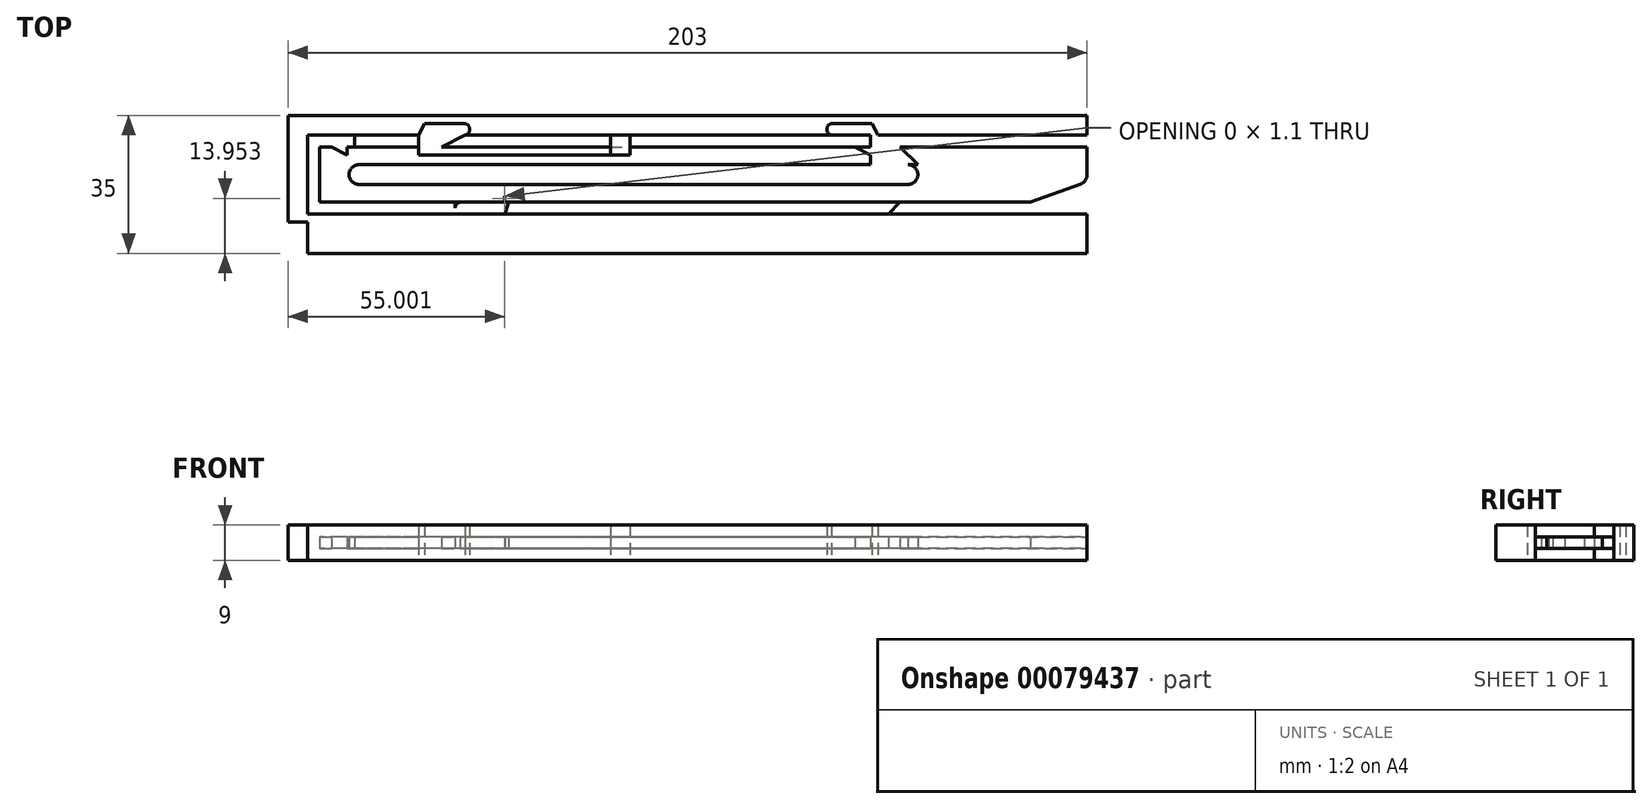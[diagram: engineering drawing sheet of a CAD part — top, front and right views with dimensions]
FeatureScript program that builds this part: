
annotation { "Feature Type Name" : "Feature", "Feature Type Description" : "" }
export const myFeature = defineFeature(function(context is Context, id is Id, definition is map)
    precondition{}
    {
        {
            var Q0;
            Q0=qCreatedBy(makeId("Top.planeOp"),FACE);
            var sketch = newSketch(context, id + "F0", { "sketchPlane" : qUnion([Q0])});
            skLineSegment(sketch, "E0.bottom", {"start": v(-77.5, 10) * mm, "end": v(77.5, 10) * mm, "construction": true});
            skLineSegment(sketch, "E0.top", {"start": v(-77.5, -10) * mm, "end": v(77.5, -10) * mm, "construction": true});
            skLineSegment(sketch, "E0.left", {"start": v(-77.5, 10) * mm, "end": v(-77.5, -10) * mm, "construction": true});
            skLineSegment(sketch, "E0.right", {"start": v(77.5, 10) * mm, "end": v(77.5, -10) * mm, "construction": true});
            skPoint(sketch, "E0.middle", {"position": v(0, 0) * mm});
            skLineSegment(sketch, "E1.bottom", {"start": v(-77.5, -2.5) * mm, "end": v(77.5, -2.5) * mm, "construction": true});
            skLineSegment(sketch, "E1.top", {"start": v(-77.5, 2.5) * mm, "end": v(77.5, 2.5) * mm, "construction": true});
            skLineSegment(sketch, "E1.left", {"start": v(-77.5, -2.5) * mm, "end": v(-77.5, 2.5) * mm, "construction": true});
            skLineSegment(sketch, "E1.right", {"start": v(77.5, -2.5) * mm, "end": v(77.5, 2.5) * mm, "construction": true});
            skLineSegment(sketch, "E2.top", {"start": v(-77.5, 7) * mm, "end": v(77.5, 7) * mm, "construction": true});
            skLineSegment(sketch, "E2.left", {"start": v(-77.5, 10) * mm, "end": v(-77.5, 7) * mm, "construction": true});
            skLineSegment(sketch, "E2.right", {"start": v(77.5, 10) * mm, "end": v(77.5, 7) * mm, "construction": true});
            skLineSegment(sketch, "E3", {"start": v(-77.5, 10) * mm, "end": v(-67.5, 7) * mm});
            skLineSegment(sketch, "E4", {"start": v(-67.5, 7) * mm, "end": v(-67.5, 10) * mm});
            skLineSegment(sketch, "E5", {"start": v(-67.5, 10) * mm, "end": v(-47.5, 10) * mm});
            skLineSegment(sketch, "E6.top", {"start": v(-77.5, -7) * mm, "end": v(77.5, -7) * mm, "construction": true});
            skLineSegment(sketch, "E6.left", {"start": v(-77.5, -10) * mm, "end": v(-77.5, -7) * mm, "construction": true});
            skLineSegment(sketch, "E6.right", {"start": v(77.5, -10) * mm, "end": v(77.5, -7) * mm, "construction": true});
            skLineSegment(sketch, "E7", {"start": v(-77.5, -10) * mm, "end": v(-77.5, -2.5) * mm});
            skLineSegment(sketch, "E8", {"start": v(77.5, -2.5) * mm, "end": v(70, -10) * mm});
            skLineSegment(sketch, "E9", {"start": v(77.5, 2.5) * mm, "end": v(70, 10) * mm});
            skLineSegment(sketch, "E10", {"start": v(70, 10) * mm, "end": v(-37.5, 10) * mm});
            skLineSegment(sketch, "E11", {"start": v(-43.17, 2.5) * mm, "end": v(-43.17, -2.5) * mm, "construction": true});
            skLineSegment(sketch, "E12", {"start": v(77.5, -2.5) * mm, "end": v(-43.17, -2.5) * mm});
            skLineSegment(sketch, "E13", {"start": v(77.5, 2.5) * mm, "end": v(-43.17, 2.5) * mm});
            skLineSegment(sketch, "E14", {"start": v(-77.5, 2.5) * mm, "end": v(-77.5, 10) * mm});
            skLineSegment(sketch, "E15", {"start": v(70, -10) * mm, "end": v(-77.5, -10) * mm});
            skLineSegment(sketch, "E16", {"start": v(-37.5, 10) * mm, "end": v(-47.5, 5) * mm});
            skLineSegment(sketch, "E17", {"start": v(-47.5, 10) * mm, "end": v(-47.5, 5) * mm});
            skArc(sketch, "E18", {"start": v(-77.5, -2.5) * mm, "mid": v(-75, 0) * mm, "end": v(-77.5, 2.5) * mm});
            skArc(sketch, "E19", {"start": v(-43.17, 2.5) * mm, "mid": v(-45.67, 0) * mm, "end": v(-43.17, -2.5) * mm});
            skSolve(sketch);
        }
        {
            var Q0;
            Q0=makeQuery(id+"F0.imprint","IMPRINT",FACE,{"disambiguationData":[TD([[makeQuery(id+"F0.imprint","IMPRINT",EDGE,{"derivedFrom":sQuery(id+"F0.wireOp",EDGE,"E3")}),-1.0]])]});
            var sketch = newSketch(context, id + "F1", { "sketchPlane" : qUnion([Q0])});
            skLineSegment(sketch, "E20.bottom", {"start": v(-161.47, 129.05) * mm, "end": v(-6.47, 129.05) * mm, "construction": true});
            skLineSegment(sketch, "E20.top", {"start": v(-161.47, 109.05) * mm, "end": v(-6.47, 109.05) * mm, "construction": true});
            skLineSegment(sketch, "E20.left", {"start": v(-161.47, 129.05) * mm, "end": v(-161.47, 109.05) * mm, "construction": true});
            skLineSegment(sketch, "E20.right", {"start": v(-6.47, 129.05) * mm, "end": v(-6.47, 109.05) * mm, "construction": true});
            skPoint(sketch, "E20.middle", {"position": v(-83.97, 119.05) * mm});
            skLineSegment(sketch, "E21.bottom", {"start": v(-161.47, 116.55) * mm, "end": v(-6.47, 116.55) * mm, "construction": true});
            skLineSegment(sketch, "E21.top", {"start": v(-161.47, 121.55) * mm, "end": v(-6.47, 121.55) * mm, "construction": true});
            skLineSegment(sketch, "E21.left", {"start": v(-161.47, 116.55) * mm, "end": v(-161.47, 121.55) * mm, "construction": true});
            skLineSegment(sketch, "E21.right", {"start": v(-6.47, 116.55) * mm, "end": v(-6.47, 121.55) * mm, "construction": true});
            skLineSegment(sketch, "E22.top", {"start": v(-161.47, 126.05) * mm, "end": v(-6.47, 126.05) * mm, "construction": true});
            skLineSegment(sketch, "E22.left", {"start": v(-161.47, 129.05) * mm, "end": v(-161.47, 126.05) * mm, "construction": true});
            skLineSegment(sketch, "E22.right", {"start": v(-6.47, 129.05) * mm, "end": v(-6.47, 126.05) * mm, "construction": true});
            skLineSegment(sketch, "E23", {"start": v(-151.47, 129.05) * mm, "end": v(-133.36, 129.05) * mm});
            skLineSegment(sketch, "E24.top", {"start": v(-161.47, 112.05) * mm, "end": v(-6.47, 112.05) * mm, "construction": true});
            skLineSegment(sketch, "E24.left", {"start": v(-161.47, 109.05) * mm, "end": v(-161.47, 112.05) * mm, "construction": true});
            skLineSegment(sketch, "E24.right", {"start": v(-6.47, 109.05) * mm, "end": v(-6.47, 112.05) * mm, "construction": true});
            skLineSegment(sketch, "E25", {"start": v(-161.47, 109.05) * mm, "end": v(-161.47, 116.55) * mm});
            skLineSegment(sketch, "E26", {"start": v(-6.47, 116.55) * mm, "end": v(-13.97, 109.05) * mm});
            skLineSegment(sketch, "E27", {"start": v(-6.47, 121.55) * mm, "end": v(-13.97, 129.05) * mm});
            skLineSegment(sketch, "E28", {"start": v(-13.97, 129.05) * mm, "end": v(-16.59, 129.05) * mm});
            skLineSegment(sketch, "E29", {"start": v(-127.14, 121.55) * mm, "end": v(-127.14, 116.55) * mm, "construction": true});
            skLineSegment(sketch, "E30", {"start": v(-6.47, 116.55) * mm, "end": v(-127.14, 116.55) * mm});
            skLineSegment(sketch, "E31", {"start": v(-6.47, 121.55) * mm, "end": v(-127.14, 121.55) * mm});
            skLineSegment(sketch, "E32", {"start": v(-161.47, 121.55) * mm, "end": v(-161.47, 129.05) * mm});
            skLineSegment(sketch, "E33", {"start": v(-13.97, 109.05) * mm, "end": v(-111.47, 109.05) * mm});
            skLineSegment(sketch, "E34", {"start": v(-121.16, 129.2) * mm, "end": v(-131.47, 124.05) * mm});
            skLineSegment(sketch, "E35", {"start": v(-131.47, 129.05) * mm, "end": v(-131.47, 124.05) * mm, "construction": true});
            skArc(sketch, "E36", {"start": v(-161.47, 116.55) * mm, "mid": v(-158.97, 119.05) * mm, "end": v(-161.47, 121.55) * mm});
            skArc(sketch, "E37", {"start": v(-127.14, 121.55) * mm, "mid": v(-129.64, 119.05) * mm, "end": v(-127.14, 116.55) * mm});
            skLineSegment(sketch, "E38.left", {"start": v(-158.47, 126.05) * mm, "end": v(-158.47, 112.05) * mm, "construction": true});
            skLineSegment(sketch, "E39", {"start": v(-158.47, 119.05) * mm, "end": v(36.53, 119.05) * mm, "construction": true});
            skLineSegment(sketch, "E40", {"start": v(-158.47, 126.05) * mm, "end": v(36.53, 126.05) * mm, "construction": true});
            skLineSegment(sketch, "E41", {"start": v(36.53, 126.05) * mm, "end": v(36.53, 112.05) * mm, "construction": true});
            skLineSegment(sketch, "E42", {"start": v(36.53, 112.05) * mm, "end": v(-158.47, 112.05) * mm, "construction": true});
            skArc(sketch, "E43", {"start": v(34.88, 116.7) * mm, "mid": v(36.53, 119.05) * mm, "end": v(34.88, 121.4) * mm});
            skLineSegment(sketch, "E44", {"start": v(34.88, 121.4) * mm, "end": v(22.1, 126.05) * mm});
            skLineSegment(sketch, "E45", {"start": v(34.88, 116.7) * mm, "end": v(22.1, 112.05) * mm});
            skArc(sketch, "E46", {"start": v(34.88, 121.4) * mm, "mid": v(31.53, 119.05) * mm, "end": v(34.88, 116.7) * mm, "construction": true});
            skLineSegment(sketch, "E47", {"start": v(-158.47, 126.05) * mm, "end": v(-133.36, 126.05) * mm});
            skLineSegment(sketch, "E48", {"start": v(-131.47, 124.05) * mm, "end": v(-127.48, 126.05) * mm});
            skLineSegment(sketch, "E49", {"start": v(-81.47, 126.05) * mm, "end": v(22.1, 126.05) * mm});
            skLineSegment(sketch, "E50", {"start": v(22.1, 112.05) * mm, "end": v(-158.47, 112.05) * mm});
            skLineSegment(sketch, "E51", {"start": v(-158.47, 126.05) * mm, "end": v(-158.47, 112.05) * mm});
            skLineSegment(sketch, "E52", {"start": v(-111.47, 126.05) * mm, "end": v(-111.47, 112.05) * mm, "construction": true});
            skLineSegment(sketch, "E53", {"start": v(-114.47, 113.55) * mm, "end": v(-158.47, 113.55) * mm, "construction": true});
            skLineSegment(sketch, "E54", {"start": v(-81.47, 124.05) * mm, "end": v(-81.47, 126.05) * mm});
            skLineSegment(sketch, "E55.trimOffspring", {"start": v(-81.47, 124.05) * mm, "end": v(27.6, 124.05) * mm, "construction": true});
            skLineSegment(sketch, "E56", {"start": v(-81.47, 124.05) * mm, "end": v(-131.47, 124.05) * mm});
            skLineSegment(sketch, "E57", {"start": v(-131.47, 126.05) * mm, "end": v(-131.47, 124.05) * mm});
            skLineSegment(sketch, "E58", {"start": v(-113.42, 114.98) * mm, "end": v(-122.97, 111.98) * mm});
            skLineSegment(sketch, "E59", {"start": v(-122.07, 109.12) * mm, "end": v(-112.52, 112.12) * mm});
            skLineSegment(sketch, "E60", {"start": v(-111.47, 112.05) * mm, "end": v(-111.47, 109.05) * mm});
            skLineSegment(sketch, "E61", {"start": v(-124.02, 112.05) * mm, "end": v(-124.02, 110.05) * mm});
            skCircle(sketch, "E62", {"center": v(-122.52, 110.55) * mm, "radius": 0.5 * mm, "construction": true});
            skCircle(sketch, "E63", {"center": v(-112.97, 113.55) * mm, "radius": 0.5 * mm, "construction": true});
            skLineSegment(sketch, "E64.0", {"start": v(-111.48, 113.5) * mm, "end": v(-117.04, 111.75) * mm, "construction": true});
            skLineSegment(sketch, "E65.0", {"start": v(-111.6, 112.93) * mm, "end": v(-116.9, 111.27) * mm, "construction": true});
            skLineSegment(sketch, "E66", {"start": v(-124.02, 109.55) * mm, "end": v(-129.02, 109.55) * mm, "construction": true});
            skLineSegment(sketch, "E67", {"start": v(-124.02, 110.05) * mm, "end": v(-139.02, 110.05) * mm});
            skLineSegment(sketch, "E68", {"start": v(-139.02, 109.55) * mm, "end": v(-139.02, 110.05) * mm});
            skLineSegment(sketch, "E69", {"start": v(-129.02, 109.05) * mm, "end": v(-129.02, 109.55) * mm});
            skLineSegment(sketch, "E70", {"start": v(-129.02, 109.55) * mm, "end": v(-139.02, 109.55) * mm});
            skLineSegment(sketch, "E71", {"start": v(-129.02, 109.05) * mm, "end": v(-161.47, 109.05) * mm});
            skLineSegment(sketch, "E72", {"start": v(-111.47, 109.05) * mm, "end": v(-129.02, 109.05) * mm, "construction": true});
            skLineSegment(sketch, "E73", {"start": v(-124.02, 110.05) * mm, "end": v(-124.02, 109.05) * mm, "construction": true});
            skArc(sketch, "E74", {"start": v(-123.72, 109.65) * mm, "mid": v(-123.52, 109.43) * mm, "end": v(-123.29, 109.26) * mm});
            skArc(sketch, "E75", {"start": v(-123.29, 109.26) * mm, "mid": v(-122.7, 109.06) * mm, "end": v(-122.07, 109.12) * mm});
            skArc(sketch, "E76", {"start": v(-121.02, 110.5) * mm, "mid": v(-121.6, 111.74) * mm, "end": v(-122.97, 111.98) * mm, "construction": true});
            skArc(sketch, "E77", {"start": v(-121.15, 109.93) * mm, "mid": v(-121.06, 110.2) * mm, "end": v(-121.02, 110.5) * mm, "construction": true});
            skLineSegment(sketch, "E78", {"start": v(-151.47, 129.05) * mm, "end": v(-151.47, 124.05) * mm});
            skLineSegment(sketch, "E79", {"start": v(-151.47, 124.05) * mm, "end": v(-161.47, 129.05) * mm});
            skPoint(sketch, "E80", {"position": v(-166.47, 104.05) * mm});
            skLineSegment(sketch, "E81", {"start": v(-166.47, 104.05) * mm, "end": v(36.53, 104.05) * mm});
            skPoint(sketch, "E82", {"position": v(-166.47, 134.05) * mm});
            skLineSegment(sketch, "E83", {"start": v(-166.47, 134.05) * mm, "end": v(36.53, 134.05) * mm});
            skLineSegment(sketch, "E84", {"start": v(36.53, 134.05) * mm, "end": v(-166.47, 134.05) * mm});
            skLineSegment(sketch, "E85", {"start": v(-166.47, 104.05) * mm, "end": v(-166.47, 134.05) * mm});
            skLineSegment(sketch, "E86", {"start": v(36.53, 104.05) * mm, "end": v(36.53, 134.05) * mm});
            skLineSegment(sketch, "E87.trimOffspring", {"start": v(-122.5, 131.89) * mm, "end": v(-131.47, 127.4) * mm});
            skLineSegment(sketch, "E88", {"start": v(-13.97, 109.05) * mm, "end": v(36.53, 109.05) * mm});
            skLineSegment(sketch, "E89", {"start": v(-13.97, 129.05) * mm, "end": v(36.53, 129.05) * mm});
            skPoint(sketch, "E90", {"position": v(-18.47, 109.05) * mm});
            skLineSegment(sketch, "E91", {"start": v(-18.47, 109.05) * mm, "end": v(-18.47, 129.05) * mm, "construction": true});
            skLineSegment(sketch, "E92", {"start": v(-166.47, 130.55) * mm, "end": v(36.53, 130.55) * mm, "construction": true});
            skLineSegment(sketch, "E93", {"start": v(-28.8, 129.2) * mm, "end": v(-18.47, 124.05) * mm});
            skLineSegment(sketch, "E94", {"start": v(-131.47, 127.4) * mm, "end": v(-18.47, 127.4) * mm, "construction": true});
            skLineSegment(sketch, "E95", {"start": v(-166.47, 132.56) * mm, "end": v(36.53, 132.56) * mm, "construction": true});
            skLineSegment(sketch, "E96", {"start": v(-18.47, 127.4) * mm, "end": v(-27.45, 131.89) * mm});
            skCircle(sketch, "E97", {"center": v(-121.83, 130.55) * mm, "radius": 1.5 * mm});
            skPoint(sketch, "E98.orphan", {"position": v(-121.16, 132.56) * mm});
            skCircle(sketch, "E99", {"center": v(-28.12, 130.55) * mm, "radius": 1.5 * mm});
            skPoint(sketch, "E100", {"position": v(-28.47, 129.05) * mm});
            skLineSegment(sketch, "E101", {"start": v(-18.47, 124.05) * mm, "end": v(-18.47, 127.4) * mm});
            skArc(sketch, "E102", {"start": v(-122.07, 109.12) * mm, "mid": v(-121.52, 109.43) * mm, "end": v(-121.15, 109.93) * mm, "construction": true});
            skArc(sketch, "E103", {"start": v(-122.97, 111.98) * mm, "mid": v(-123.95, 111) * mm, "end": v(-123.72, 109.65) * mm});
            skArc(sketch, "E104", {"start": v(-113.42, 114.98) * mm, "mid": v(-114.4, 113.1) * mm, "end": v(-112.52, 112.12) * mm, "construction": true});
            skArc(sketch, "E105", {"start": v(-112.52, 112.12) * mm, "mid": v(-111.54, 114) * mm, "end": v(-113.42, 114.98) * mm});
            skLineSegment(sketch, "E106", {"start": v(-116.9, 111.27) * mm, "end": v(-117.04, 111.75) * mm});
            skLineSegment(sketch, "E107", {"start": v(-116.9, 111.27) * mm, "end": v(-123.29, 109.26) * mm});
            skLineSegment(sketch, "E108", {"start": v(-117.04, 111.75) * mm, "end": v(-123.72, 109.65) * mm});
            skCircle(sketch, "E109", {"center": v(-121.83, 130.55) * mm, "radius": 11.63 * mm, "construction": true});
            skLineSegment(sketch, "E110", {"start": v(-133.36, 129.05) * mm, "end": v(-133.36, 124.05) * mm});
            skLineSegment(sketch, "E111", {"start": v(-133.36, 124.05) * mm, "end": v(-131.47, 124.05) * mm});
            skLineSegment(sketch, "E112", {"start": v(-133.36, 126.05) * mm, "end": v(-131.47, 126.05) * mm, "construction": true});
            skLineSegment(sketch, "E113", {"start": v(-133.36, 129.05) * mm, "end": v(-131.47, 129.05) * mm, "construction": true});
            skCircle(sketch, "E114", {"center": v(-28.12, 130.55) * mm, "radius": 11.63 * mm, "construction": true});
            skLineSegment(sketch, "E115", {"start": v(-29.62, 129.05) * mm, "end": v(-29.62, 132.05) * mm});
            skLineSegment(sketch, "E116", {"start": v(-29.62, 132.05) * mm, "end": v(-16.59, 132.05) * mm});
            skPoint(sketch, "E117", {"position": v(-16.59, 129.05) * mm});
            skLineSegment(sketch, "E118", {"start": v(-16.59, 129.05) * mm, "end": v(-16.59, 132.05) * mm});
            skLineSegment(sketch, "E119", {"start": v(-121.83, 132.05) * mm, "end": v(-133.36, 132.05) * mm});
            skLineSegment(sketch, "E120", {"start": v(-133.36, 129.05) * mm, "end": v(-133.36, 132.05) * mm});
            skLineSegment(sketch, "E121", {"start": v(-120.33, 132.05) * mm, "end": v(-120.33, 129.05) * mm});
            skLineSegment(sketch, "E122", {"start": v(-120.33, 132.05) * mm, "end": v(-121.83, 132.05) * mm});
            skLineSegment(sketch, "E123", {"start": v(-120.33, 129.05) * mm, "end": v(-121.47, 129.05) * mm, "construction": true});
            skLineSegment(sketch, "E124", {"start": v(-29.62, 129.05) * mm, "end": v(-120.33, 129.05) * mm});
            skLineSegment(sketch, "E125", {"start": v(-16.59, 129.05) * mm, "end": v(-29.62, 129.05) * mm, "construction": true});
            skLineSegment(sketch, "E126.bottom", {"start": v(-216.14, 254.87) * mm, "end": v(-61.14, 254.87) * mm});
            skLineSegment(sketch, "E126.top", {"start": v(-216.14, 234.87) * mm, "end": v(-61.14, 234.87) * mm, "construction": true});
            skLineSegment(sketch, "E126.left", {"start": v(-216.14, 254.87) * mm, "end": v(-216.14, 234.87) * mm});
            skLineSegment(sketch, "E126.right", {"start": v(-61.14, 254.87) * mm, "end": v(-61.14, 234.87) * mm, "construction": true});
            skPoint(sketch, "E126.middle", {"position": v(-138.64, 244.87) * mm});
            skLineSegment(sketch, "E127.bottom", {"start": v(-216.14, 242.37) * mm, "end": v(-61.14, 242.37) * mm, "construction": true});
            skLineSegment(sketch, "E127.top", {"start": v(-216.14, 247.37) * mm, "end": v(-61.14, 247.37) * mm, "construction": true});
            skLineSegment(sketch, "E127.left", {"start": v(-216.14, 242.37) * mm, "end": v(-216.14, 247.37) * mm, "construction": true});
            skLineSegment(sketch, "E127.right", {"start": v(-61.14, 242.37) * mm, "end": v(-61.14, 247.37) * mm});
            skLineSegment(sketch, "E128.bottom", {"start": v(-216.14, 254.87) * mm, "end": v(-61.14, 254.87) * mm, "construction": true});
            skLineSegment(sketch, "E128.top", {"start": v(-216.14, 251.87) * mm, "end": v(-61.14, 251.87) * mm, "construction": true});
            skLineSegment(sketch, "E128.left", {"start": v(-216.14, 254.87) * mm, "end": v(-216.14, 251.87) * mm, "construction": true});
            skLineSegment(sketch, "E128.right", {"start": v(-61.14, 254.87) * mm, "end": v(-61.14, 251.87) * mm, "construction": true});
            skLineSegment(sketch, "E129", {"start": v(-206.14, 254.87) * mm, "end": v(-188.03, 254.87) * mm});
            skLineSegment(sketch, "E130.top", {"start": v(-216.14, 237.87) * mm, "end": v(-61.14, 237.87) * mm, "construction": true});
            skLineSegment(sketch, "E130.left", {"start": v(-216.14, 234.87) * mm, "end": v(-216.14, 237.87) * mm, "construction": true});
            skLineSegment(sketch, "E130.right", {"start": v(-61.14, 234.87) * mm, "end": v(-61.14, 237.87) * mm, "construction": true});
            skLineSegment(sketch, "E131", {"start": v(-216.14, 234.87) * mm, "end": v(-216.14, 242.37) * mm});
            skLineSegment(sketch, "E132", {"start": v(-61.14, 242.37) * mm, "end": v(-68.64, 234.87) * mm});
            skLineSegment(sketch, "E133", {"start": v(-61.14, 247.37) * mm, "end": v(-68.64, 254.87) * mm});
            skLineSegment(sketch, "E134", {"start": v(-68.64, 254.87) * mm, "end": v(-71.25, 254.87) * mm});
            skLineSegment(sketch, "E135", {"start": v(-181.8, 247.37) * mm, "end": v(-181.8, 242.37) * mm, "construction": true});
            skLineSegment(sketch, "E136", {"start": v(-61.14, 242.37) * mm, "end": v(-181.8, 242.37) * mm});
            skLineSegment(sketch, "E137", {"start": v(-61.14, 247.37) * mm, "end": v(-181.8, 247.37) * mm});
            skLineSegment(sketch, "E138", {"start": v(-216.14, 247.37) * mm, "end": v(-216.14, 254.87) * mm});
            skLineSegment(sketch, "E139", {"start": v(-68.64, 234.87) * mm, "end": v(-166.14, 234.87) * mm});
            skLineSegment(sketch, "E140", {"start": v(-175.82, 255.03) * mm, "end": v(-186.14, 249.87) * mm});
            skLineSegment(sketch, "E141", {"start": v(-186.14, 254.87) * mm, "end": v(-186.14, 249.87) * mm, "construction": true});
            skArc(sketch, "E142", {"start": v(-216.14, 242.37) * mm, "mid": v(-213.64, 244.87) * mm, "end": v(-216.14, 247.37) * mm});
            skArc(sketch, "E143", {"start": v(-181.8, 247.37) * mm, "mid": v(-184.3, 244.87) * mm, "end": v(-181.8, 242.37) * mm, "construction": true});
            skLineSegment(sketch, "E144.left", {"start": v(-213.14, 251.87) * mm, "end": v(-213.14, 237.87) * mm, "construction": true});
            skLineSegment(sketch, "E145", {"start": v(-213.14, 244.87) * mm, "end": v(-18.14, 244.87) * mm, "construction": true});
            skLineSegment(sketch, "E146", {"start": v(-213.14, 251.87) * mm, "end": v(-136.93, 251.87) * mm});
            skLineSegment(sketch, "E147", {"start": v(-18.14, 251.87) * mm, "end": v(-18.14, 237.87) * mm, "construction": true});
            skLineSegment(sketch, "E148", {"start": v(-18.14, 237.87) * mm, "end": v(-213.14, 237.87) * mm, "construction": true});
            skArc(sketch, "E149", {"start": v(-19.78, 242.52) * mm, "mid": v(-18.14, 244.87) * mm, "end": v(-19.78, 247.22) * mm});
            skLineSegment(sketch, "E150", {"start": v(-19.78, 247.22) * mm, "end": v(-32.56, 251.87) * mm});
            skLineSegment(sketch, "E151", {"start": v(-19.78, 242.52) * mm, "end": v(-32.56, 237.87) * mm});
            skArc(sketch, "E152", {"start": v(-19.78, 247.22) * mm, "mid": v(-23.14, 244.87) * mm, "end": v(-19.78, 242.52) * mm, "construction": true});
            skLineSegment(sketch, "E153", {"start": v(-213.14, 251.87) * mm, "end": v(-188.03, 251.87) * mm});
            skLineSegment(sketch, "E154", {"start": v(-186.14, 249.87) * mm, "end": v(-182.14, 251.87) * mm});
            skLineSegment(sketch, "E155", {"start": v(-136.14, 251.87) * mm, "end": v(-134.25, 251.87) * mm});
            skLineSegment(sketch, "E156", {"start": v(-32.56, 237.87) * mm, "end": v(-213.14, 237.87) * mm});
            skLineSegment(sketch, "E157", {"start": v(-213.14, 251.87) * mm, "end": v(-213.14, 237.87) * mm});
            skLineSegment(sketch, "E158", {"start": v(-166.14, 251.87) * mm, "end": v(-166.14, 237.87) * mm, "construction": true});
            skLineSegment(sketch, "E159", {"start": v(-169.14, 239.37) * mm, "end": v(-213.14, 239.37) * mm, "construction": true});
            skLineSegment(sketch, "E160", {"start": v(-136.14, 249.87) * mm, "end": v(-136.14, 251.87) * mm, "construction": true});
            skLineSegment(sketch, "E161.trimOffspring", {"start": v(-136.14, 249.87) * mm, "end": v(-134.25, 249.87) * mm});
            skLineSegment(sketch, "E162", {"start": v(-136.14, 249.87) * mm, "end": v(-136.93, 249.87) * mm});
            skLineSegment(sketch, "E163", {"start": v(-186.14, 251.87) * mm, "end": v(-186.14, 249.87) * mm});
            skLineSegment(sketch, "E164", {"start": v(-168.09, 240.8) * mm, "end": v(-177.63, 237.8) * mm});
            skLineSegment(sketch, "E165", {"start": v(-176.73, 234.94) * mm, "end": v(-167.19, 237.94) * mm});
            skLineSegment(sketch, "E166", {"start": v(-166.14, 237.87) * mm, "end": v(-166.14, 234.87) * mm, "construction": true});
            skLineSegment(sketch, "E167", {"start": v(-178.68, 237.87) * mm, "end": v(-178.68, 235.87) * mm});
            skCircle(sketch, "E168", {"center": v(-177.18, 236.37) * mm, "radius": 0.5 * mm});
            skCircle(sketch, "E169", {"center": v(-167.64, 239.37) * mm, "radius": 0.5 * mm});
            skLineSegment(sketch, "E170.0", {"start": v(-166.14, 239.32) * mm, "end": v(-171.7, 237.57) * mm, "construction": true});
            skLineSegment(sketch, "E171.0", {"start": v(-166.27, 238.75) * mm, "end": v(-171.55, 237.1) * mm, "construction": true});
            skLineSegment(sketch, "E172", {"start": v(-178.68, 235.37) * mm, "end": v(-183.68, 235.37) * mm, "construction": true});
            skLineSegment(sketch, "E173", {"start": v(-178.68, 235.87) * mm, "end": v(-193.68, 235.87) * mm});
            skLineSegment(sketch, "E174", {"start": v(-183.68, 235.37) * mm, "end": v(-193.68, 235.37) * mm});
            skLineSegment(sketch, "E175", {"start": v(-183.68, 234.87) * mm, "end": v(-216.14, 234.87) * mm});
            skLineSegment(sketch, "E176", {"start": v(-166.14, 234.87) * mm, "end": v(-183.68, 234.87) * mm, "construction": true});
            skArc(sketch, "E177", {"start": v(-178.38, 235.47) * mm, "mid": v(-178.18, 235.26) * mm, "end": v(-177.95, 235.08) * mm});
            skArc(sketch, "E178", {"start": v(-177.95, 235.08) * mm, "mid": v(-177.36, 234.88) * mm, "end": v(-176.73, 234.94) * mm});
            skArc(sketch, "E179", {"start": v(-175.68, 236.32) * mm, "mid": v(-176.27, 237.57) * mm, "end": v(-177.63, 237.8) * mm});
            skArc(sketch, "E180", {"start": v(-175.82, 235.75) * mm, "mid": v(-175.72, 236.03) * mm, "end": v(-175.68, 236.32) * mm});
            skLineSegment(sketch, "E181", {"start": v(-206.14, 254.87) * mm, "end": v(-206.14, 249.87) * mm});
            skLineSegment(sketch, "E182", {"start": v(-206.14, 249.87) * mm, "end": v(-216.14, 254.87) * mm});
            skPoint(sketch, "E183", {"position": v(-221.14, 232.87) * mm});
            skLineSegment(sketch, "E184", {"start": v(-221.14, 232.87) * mm, "end": v(-18.14, 232.87) * mm});
            skPoint(sketch, "E185", {"position": v(-221.14, 259.87) * mm});
            skLineSegment(sketch, "E186", {"start": v(-221.14, 259.87) * mm, "end": v(-18.14, 259.87) * mm});
            skLineSegment(sketch, "E187", {"start": v(-18.14, 259.87) * mm, "end": v(-221.14, 259.87) * mm});
            skLineSegment(sketch, "E188", {"start": v(-221.14, 232.87) * mm, "end": v(-221.14, 259.87) * mm});
            skLineSegment(sketch, "E189", {"start": v(-18.14, 232.87) * mm, "end": v(-18.14, 259.87) * mm});
            skLineSegment(sketch, "E190.trimOffspring", {"start": v(-177.16, 257.71) * mm, "end": v(-186.14, 253.23) * mm});
            skLineSegment(sketch, "E191", {"start": v(-68.64, 234.87) * mm, "end": v(-18.14, 234.87) * mm});
            skLineSegment(sketch, "E192", {"start": v(-68.64, 254.87) * mm, "end": v(-18.14, 254.87) * mm});
            skPoint(sketch, "E193", {"position": v(-73.14, 234.87) * mm});
            skLineSegment(sketch, "E194", {"start": v(-73.14, 234.87) * mm, "end": v(-73.14, 254.87) * mm});
            skLineSegment(sketch, "E195", {"start": v(-221.14, 256.37) * mm, "end": v(-18.14, 256.37) * mm, "construction": true});
            skLineSegment(sketch, "E196", {"start": v(-83.46, 255.03) * mm, "end": v(-73.14, 249.87) * mm});
            skLineSegment(sketch, "E197", {"start": v(-186.14, 253.23) * mm, "end": v(-73.14, 253.23) * mm, "construction": true});
            skLineSegment(sketch, "E198", {"start": v(-221.14, 258.39) * mm, "end": v(-18.14, 258.39) * mm, "construction": true});
            skLineSegment(sketch, "E199", {"start": v(-73.14, 253.23) * mm, "end": v(-82.11, 257.71) * mm});
            skCircle(sketch, "E200", {"center": v(-176.5, 256.37) * mm, "radius": 1.5 * mm});
            skPoint(sketch, "E201.orphan", {"position": v(-175.82, 258.39) * mm});
            skCircle(sketch, "E202", {"center": v(-82.78, 256.37) * mm, "radius": 1.5 * mm});
            skPoint(sketch, "E203", {"position": v(-83.14, 254.87) * mm});
            skLineSegment(sketch, "E204", {"start": v(-73.14, 249.87) * mm, "end": v(-73.14, 253.23) * mm});
            skArc(sketch, "E205", {"start": v(-176.73, 234.94) * mm, "mid": v(-176.19, 235.25) * mm, "end": v(-175.82, 235.75) * mm});
            skArc(sketch, "E206", {"start": v(-177.63, 237.8) * mm, "mid": v(-178.61, 236.83) * mm, "end": v(-178.38, 235.47) * mm});
            skArc(sketch, "E207", {"start": v(-168.09, 240.8) * mm, "mid": v(-169.07, 238.92) * mm, "end": v(-167.19, 237.94) * mm});
            skArc(sketch, "E208", {"start": v(-167.19, 237.94) * mm, "mid": v(-166.2, 239.82) * mm, "end": v(-168.09, 240.8) * mm});
            skLineSegment(sketch, "E209", {"start": v(-171.55, 237.1) * mm, "end": v(-171.7, 237.57) * mm});
            skLineSegment(sketch, "E210", {"start": v(-171.55, 237.1) * mm, "end": v(-177.95, 235.08) * mm});
            skLineSegment(sketch, "E211", {"start": v(-171.7, 237.57) * mm, "end": v(-178.38, 235.47) * mm});
            skLineSegment(sketch, "E212", {"start": v(-188.03, 254.87) * mm, "end": v(-188.03, 249.87) * mm});
            skLineSegment(sketch, "E213", {"start": v(-188.03, 249.87) * mm, "end": v(-186.14, 249.87) * mm});
            skLineSegment(sketch, "E214", {"start": v(-188.03, 251.87) * mm, "end": v(-186.14, 251.87) * mm, "construction": true});
            skLineSegment(sketch, "E215", {"start": v(-188.03, 254.87) * mm, "end": v(-186.14, 254.87) * mm, "construction": true});
            skLineSegment(sketch, "E216", {"start": v(-84.28, 254.87) * mm, "end": v(-84.28, 257.87) * mm});
            skLineSegment(sketch, "E217", {"start": v(-84.28, 257.87) * mm, "end": v(-71.25, 257.87) * mm});
            skPoint(sketch, "E218", {"position": v(-71.25, 254.87) * mm});
            skLineSegment(sketch, "E219", {"start": v(-71.25, 254.87) * mm, "end": v(-71.25, 257.87) * mm});
            skLineSegment(sketch, "E220", {"start": v(-176.5, 257.87) * mm, "end": v(-188.03, 257.87) * mm});
            skLineSegment(sketch, "E221", {"start": v(-188.03, 254.87) * mm, "end": v(-188.03, 257.87) * mm});
            skLineSegment(sketch, "E222", {"start": v(-175, 257.87) * mm, "end": v(-175, 254.87) * mm});
            skLineSegment(sketch, "E223", {"start": v(-175, 257.87) * mm, "end": v(-176.5, 257.87) * mm});
            skLineSegment(sketch, "E224", {"start": v(-175, 254.87) * mm, "end": v(-176.14, 254.87) * mm, "construction": true});
            skLineSegment(sketch, "E225", {"start": v(-84.28, 254.87) * mm, "end": v(-175, 254.87) * mm});
            skLineSegment(sketch, "E226", {"start": v(-71.25, 254.87) * mm, "end": v(-84.28, 254.87) * mm, "construction": true});
            skLineSegment(sketch, "E227", {"start": v(-166.14, 234.87) * mm, "end": v(-183.68, 234.87) * mm});
            skLineSegment(sketch, "E228", {"start": v(-183.68, 235.37) * mm, "end": v(-183.68, 234.87) * mm});
            skLineSegment(sketch, "E229", {"start": v(-193.68, 235.87) * mm, "end": v(-193.68, 235.37) * mm});
            skLineSegment(sketch, "E230", {"start": v(-166.14, 239.32) * mm, "end": v(-166.14, 237.87) * mm});
            skLineSegment(sketch, "E231", {"start": v(-178.68, 235.87) * mm, "end": v(-178.68, 234.87) * mm});
            skLineSegment(sketch, "E232", {"start": v(-168.09, 240.8) * mm, "end": v(-166.14, 241.42) * mm});
            skLineSegment(sketch, "E233", {"start": v(-167.19, 237.94) * mm, "end": v(-166.14, 238.27) * mm});
            skLineSegment(sketch, "E234", {"start": v(-166.14, 241.42) * mm, "end": v(-166.14, 238.27) * mm});
            skLineSegment(sketch, "E235", {"start": v(-165.04, 241.42) * mm, "end": v(-166.14, 241.42) * mm});
            skCircle(sketch, "E236", {"center": v(-176.5, 256.37) * mm, "radius": 10.15 * mm, "construction": true});
            skLineSegment(sketch, "E237", {"start": v(-188.03, 254.87) * mm, "end": v(-186.53, 257.87) * mm});
            skCircle(sketch, "E238", {"center": v(-177.18, 236.37) * mm, "radius": 11.2 * mm, "construction": true});
            skPoint(sketch, "E239", {"position": v(-165.13, 237.87) * mm});
            skPoint(sketch, "E240", {"position": v(-166.08, 234.87) * mm});
            skLineSegment(sketch, "E241", {"start": v(-165.13, 237.87) * mm, "end": v(-166.08, 234.87) * mm});
            skLineSegment(sketch, "E242", {"start": v(-165.13, 241.42) * mm, "end": v(-165.13, 234.87) * mm});
            skCircle(sketch, "E243", {"center": v(-82.78, 256.37) * mm, "radius": 10.15 * mm, "construction": true});
            skLineSegment(sketch, "E244", {"start": v(-71.25, 254.87) * mm, "end": v(-72.75, 257.87) * mm});
            skArc(sketch, "E245", {"start": v(-186.14, 249.87) * mm, "mid": v(-165.61, 260.48) * mm, "end": v(-188.03, 254.87) * mm, "construction": true});
            skArc(sketch, "E246", {"start": v(-188.03, 254.87) * mm, "mid": v(-187.37, 252.26) * mm, "end": v(-186.14, 249.87) * mm});
            skArc(sketch, "E247", {"start": v(-166.14, 241.42) * mm, "mid": v(-188.86, 233.06) * mm, "end": v(-165.13, 237.87) * mm, "construction": true});
            skArc(sketch, "E248", {"start": v(-165.13, 237.87) * mm, "mid": v(-165.5, 239.68) * mm, "end": v(-166.14, 241.42) * mm});
            skArc(sketch, "E249", {"start": v(-73.14, 249.87) * mm, "mid": v(-71.9, 252.26) * mm, "end": v(-71.25, 254.87) * mm});
            skArc(sketch, "E250", {"start": v(-71.25, 254.87) * mm, "mid": v(-93.67, 260.48) * mm, "end": v(-73.14, 249.87) * mm, "construction": true});
            skLineSegment(sketch, "E251", {"start": v(-165.04, 219.99) * mm, "end": v(-216.14, 219.99) * mm, "construction": true});
            skLineSegment(sketch, "E252", {"start": v(-134.25, 249.87) * mm, "end": v(-27.07, 249.87) * mm, "construction": true});
            skLineSegment(sketch, "E253", {"start": v(-136.93, 249.87) * mm, "end": v(-186.14, 249.87) * mm});
            skLineSegment(sketch, "E254", {"start": v(-134.25, 251.87) * mm, "end": v(-32.56, 251.87) * mm});
            skLineSegment(sketch, "E255", {"start": v(-136.93, 251.87) * mm, "end": v(-18.14, 251.87) * mm});
            skLineSegment(sketch, "E256", {"start": v(-134.25, 249.87) * mm, "end": v(-134.25, 251.87) * mm});
            skLineSegment(sketch, "E257", {"start": v(-188.03, 270.85) * mm, "end": v(-166.14, 270.85) * mm, "construction": true});
            skLineSegment(sketch, "E258", {"start": v(-166.14, 270.85) * mm, "end": v(-144.25, 270.85) * mm, "construction": true});
            skLineSegment(sketch, "E259", {"start": v(-144.25, 270.85) * mm, "end": v(-139.25, 270.85) * mm, "construction": true});
            skLineSegment(sketch, "E260", {"start": v(-139.25, 249.87) * mm, "end": v(-139.25, 251.87) * mm});
            skLineSegment(sketch, "E261", {"start": v(-134.25, 251.87) * mm, "end": v(-134.25, 254.87) * mm});
            skLineSegment(sketch, "E262", {"start": v(-139.25, 251.87) * mm, "end": v(-139.25, 254.87) * mm});
            skCircle(sketch, "E263", {"center": v(-177.18, 236.37) * mm, "radius": 10 * mm, "construction": true});
            skPoint(sketch, "E264", {"position": v(-167.3, 234.87) * mm});
            skCircle(sketch, "E265", {"center": v(-167.18, 236.37) * mm, "radius": 1.5 * mm});
            skArc(sketch, "E266", {"start": v(-169.07, 238.92) * mm, "mid": v(-185.67, 235.83) * mm, "end": v(-168.81, 234.87) * mm, "construction": true});
            skArc(sketch, "E267", {"start": v(-168.68, 236.37) * mm, "mid": v(-168.78, 237.66) * mm, "end": v(-169.07, 238.92) * mm});
            skArc(sketch, "E268", {"start": v(-166.2, 239.82) * mm, "mid": v(-188.64, 235.37) * mm, "end": v(-165.78, 234.87) * mm, "construction": true});
            skArc(sketch, "E269", {"start": v(-165.68, 236.37) * mm, "mid": v(-165.81, 238.12) * mm, "end": v(-166.2, 239.82) * mm});
            skCircle(sketch, "E270", {"center": v(-176.5, 256.37) * mm, "radius": 0.5 * mm});
            skCircle(sketch, "E271", {"center": v(-82.78, 256.37) * mm, "radius": 0.5 * mm});
            skArc(sketch, "E272", {"start": v(-168.81, 234.87) * mm, "mid": v(-168.71, 235.62) * mm, "end": v(-168.68, 236.37) * mm});
            skArc(sketch, "E273", {"start": v(-165.78, 234.87) * mm, "mid": v(-165.7, 235.62) * mm, "end": v(-165.68, 236.37) * mm});
            skLineSegment(sketch, "E274.trimOffspring", {"start": v(-175.03, 256.37) * mm, "end": v(-175, 256.4) * mm});
            skLineSegment(sketch, "E275", {"start": v(-206.14, 249.87) * mm, "end": v(-204.25, 249.87) * mm});
            skLineSegment(sketch, "E276", {"start": v(-204.25, 249.87) * mm, "end": v(-204.25, 254.87) * mm});
            skLineSegment(sketch, "E277", {"start": v(-186.14, 249.87) * mm, "end": v(-186.14, 253.23) * mm});
            skLineSegment(sketch, "E278", {"start": v(-221.14, 232.87) * mm, "end": v(-221.14, 227.87) * mm});
            skLineSegment(sketch, "E279", {"start": v(-221.14, 227.87) * mm, "end": v(-221.14, 224.87) * mm});
            skLineSegment(sketch, "E280", {"start": v(-221.14, 227.87) * mm, "end": v(-18.14, 227.87) * mm});
            skLineSegment(sketch, "E281", {"start": v(-221.14, 224.87) * mm, "end": v(-221.14, 232.87) * mm});
            skLineSegment(sketch, "E282", {"start": v(-221.14, 224.87) * mm, "end": v(-18.14, 224.87) * mm});
            skLineSegment(sketch, "E283", {"start": v(-18.14, 224.87) * mm, "end": v(-18.14, 232.87) * mm});
            skLineSegment(sketch, "E284", {"start": v(-216.14, 234.87) * mm, "end": v(-216.14, 224.87) * mm});
            skLineSegment(sketch, "E285", {"start": v(-23.14, 224.87) * mm, "end": v(-23.14, 232.87) * mm});
            skArc(sketch, "E286", {"start": v(-63.64, 242.37) * mm, "mid": v(-61.14, 244.87) * mm, "end": v(-63.64, 247.37) * mm});
            skLineSegment(sketch, "E287", {"start": v(-63.64, 247.37) * mm, "end": v(-63.64, 242.37) * mm, "construction": true});
            skPoint(sketch, "E288", {"position": v(-203.14, 244.87) * mm});
            skArc(sketch, "E289", {"start": v(-203.14, 247.37) * mm, "mid": v(-205.64, 244.87) * mm, "end": v(-203.14, 242.37) * mm});
            skLineSegment(sketch, "E290", {"start": v(-203.14, 242.37) * mm, "end": v(-181.8, 242.37) * mm});
            skLineSegment(sketch, "E291", {"start": v(-181.8, 247.37) * mm, "end": v(-203.14, 247.37) * mm});
            skSolve(sketch);
        }
        {
            var Q0;
            {var subQ1=sQuery(id+"F1.wireOp",EDGE,"E129");var subQ3=sQuery(id+"F1.wireOp",EDGE,"E276");var subQ4=makeQuery(id+"F1.imprint","INTERSECT",VERTEX,{"derivedFrom":[subQ1,subQ3]});Q0=makeQuery(id+"F1.imprint","IMPRINT",FACE,{"disambiguationData":[TD([[makeQuery(id+"F1.imprint","IMPRINT",EDGE,{"disambiguationData":[TD([[subQ4,1.0]])],"derivedFrom":subQ3}),-1.0]])]});}
            var Q1;
            {var subQ0=sQuery(id+"F1.wireOp",EDGE,"E262");Q1=makeQuery(id+"F1.imprint","IMPRINT",FACE,{"disambiguationData":[TD([[makeQuery(id+"F1.imprint","IMPRINT",EDGE,{"derivedFrom":subQ0}),1.0]])]});}
            var Q2;
            {var subQ3=sQuery(id+"F1.wireOp",EDGE,"E261");Q2=makeQuery(id+"F1.imprint","IMPRINT",FACE,{"disambiguationData":[TD([[makeQuery(id+"F1.imprint","IMPRINT",EDGE,{"derivedFrom":subQ3}),-1.0]])]});}
            var Q3;
            Q3=makeQuery(id+"F1.imprint","IMPRINT",FACE,{"disambiguationData":[TD([[makeQuery(id+"F1.imprint","IMPRINT",EDGE,{"derivedFrom":sQuery(id+"F1.wireOp",EDGE,"E131")}),-1.0]])]});
            var Q4;
            {var subQ0=sQuery(id+"F1.wireOp",EDGE,"E194");var subQ1=sQuery(id+"F1.wireOp",EDGE,"E139");var subQ2=makeQuery(id+"F1.imprint","INTERSECT",VERTEX,{"derivedFrom":[subQ1,subQ0]});Q4=makeQuery(id+"F1.imprint","IMPRINT",FACE,{"disambiguationData":[TD([[makeQuery(id+"F1.imprint","IMPRINT",EDGE,{"disambiguationData":[TD([[subQ2,-1.0]])],"derivedFrom":subQ1}),-1.0]])]});}
            var Q5;
            {var subQ0=sQuery(id+"F1.wireOp",EDGE,"E241");var subQ1=sQuery(id+"F1.wireOp",EDGE,"E139");var subQ2=makeQuery(id+"F1.imprint","INTERSECT",VERTEX,{"derivedFrom":[subQ1,subQ0]});Q5=makeQuery(id+"F1.imprint","IMPRINT",FACE,{"disambiguationData":[TD([[makeQuery(id+"F1.imprint","IMPRINT",EDGE,{"disambiguationData":[TD([[subQ2,1.0]])],"derivedFrom":subQ1}),-1.0]])]});}
            var Q6;
            {var subQ1=sQuery(id+"F1.wireOp",EDGE,"E132");var subQ3=sQuery(id+"F1.wireOp",EDGE,"E156");var subQ4=makeQuery(id+"F1.imprint","INTERSECT",VERTEX,{"derivedFrom":[subQ1,subQ3]});Q6=makeQuery(id+"F1.imprint","IMPRINT",FACE,{"disambiguationData":[TD([[makeQuery(id+"F1.imprint","IMPRINT",EDGE,{"disambiguationData":[TD([[subQ4,-1.0]])],"derivedFrom":subQ3}),1.0]])]});}
            var Q7;
            {var subQ0=sQuery(id+"F1.wireOp",EDGE,"E134");Q7=makeQuery(id+"F1.imprint","IMPRINT",FACE,{"disambiguationData":[TD([[makeQuery(id+"F1.imprint","IMPRINT",EDGE,{"derivedFrom":subQ0}),1.0]])]});}
            var Q8;
            {var subQ3=sQuery(id+"F1.wireOp",EDGE,"E126.bottom");var subQ6=sQuery(id+"F1.wireOp",EDGE,"E196");var subQ7=makeQuery(id+"F1.imprint","INTERSECT",VERTEX,{"derivedFrom":[subQ3,subQ6]});Q8=makeQuery(id+"F1.imprint","IMPRINT",FACE,{"disambiguationData":[TD([[makeQuery(id+"F1.imprint","IMPRINT",EDGE,{"disambiguationData":[TD([[subQ7,-1.0]])],"derivedFrom":subQ3}),-1.0]])]});}
            var Q9;
            {var subQ0=sQuery(id+"F1.wireOp",EDGE,"E194");var subQ1=sQuery(id+"F1.wireOp",EDGE,"E126.bottom");var subQ2=makeQuery(id+"F1.imprint","INTERSECT",VERTEX,{"derivedFrom":[subQ1,subQ0]});Q9=makeQuery(id+"F1.imprint","IMPRINT",FACE,{"disambiguationData":[TD([[makeQuery(id+"F1.imprint","IMPRINT",EDGE,{"disambiguationData":[TD([[subQ2,1.0]])],"derivedFrom":subQ1}),-1.0]])]});}
            var Q10;
            {var subQ3=sQuery(id+"F1.wireOp",EDGE,"E255");var subQ5=sQuery(id+"F1.wireOp",EDGE,"E204");var subQ8=makeQuery(id+"F1.imprint","INTERSECT",VERTEX,{"derivedFrom":[subQ5,subQ3]});Q10=makeQuery(id+"F1.imprint","IMPRINT",FACE,{"disambiguationData":[TD([[makeQuery(id+"F1.imprint","IMPRINT",EDGE,{"disambiguationData":[TD([[subQ8,-1.0]])],"derivedFrom":subQ3}),1.0]])]});}
            var Q11;
            {var subQ0=sQuery(id+"F1.wireOp",EDGE,"E167");var subQ1=sQuery(id+"F1.wireOp",EDGE,"E156");var subQ2=makeQuery(id+"F1.imprint","INTERSECT",VERTEX,{"derivedFrom":[subQ1,subQ0]});Q11=makeQuery(id+"F1.imprint","IMPRINT",FACE,{"disambiguationData":[TD([[makeQuery(id+"F1.imprint","IMPRINT",EDGE,{"disambiguationData":[TD([[subQ2,1.0]])],"derivedFrom":subQ1}),1.0]])]});}
            var Q12;
            {var subQ0=sQuery(id+"F1.wireOp",EDGE,"E242");var subQ1=sQuery(id+"F1.wireOp",EDGE,"E139");var subQ2=makeQuery(id+"F1.imprint","INTERSECT",VERTEX,{"derivedFrom":[subQ1,subQ0]});Q12=makeQuery(id+"F1.imprint","IMPRINT",FACE,{"disambiguationData":[TD([[makeQuery(id+"F1.imprint","IMPRINT",EDGE,{"disambiguationData":[TD([[subQ2,-1.0]])],"derivedFrom":subQ1}),-1.0]])]});}
            extrude(context, id + "F2", {"entities" : qUnion([Q0, Q1, Q2, Q3, Q4, Q5, Q6, Q7, Q8, Q9, Q10, Q11, Q12]), "depth" : 3 * mm});
        }
        {
            var Q0;
            Q0=makeQuery(id+"F2.opExtrude","SWEPT_BODY",BODY,{"disambiguationData":[OSD([sQuery(id+"F1.wireOp",EDGE,"E126.bottom"),sQuery(id+"F1.wireOp",EDGE,"E133"),sQuery(id+"F1.wireOp",EDGE,"E134"),sQuery(id+"F1.wireOp",EDGE,"E140"),sQuery(id+"F1.wireOp",EDGE,"E146"),sQuery(id+"F1.wireOp",EDGE,"E155"),sQuery(id+"F1.wireOp",EDGE,"E225")])]});
            var Q1;
            Q1=makeQuery(id+"F2.opExtrude","SWEPT_BODY",BODY,{"disambiguationData":[OSD([sQuery(id+"F1.wireOp",EDGE,"E129"),sQuery(id+"F1.wireOp",EDGE,"E153"),sQuery(id+"F1.wireOp",EDGE,"E181"),sQuery(id+"F1.wireOp",EDGE,"E212")])]});
            var Q2;
            Q2=makeQuery(id+"F2.opExtrude","SWEPT_BODY",BODY,{"disambiguationData":[OSD([sQuery(id+"F1.wireOp",EDGE,"E131"),sQuery(id+"F1.wireOp",EDGE,"E138"),sQuery(id+"F1.wireOp",EDGE,"E142"),sQuery(id+"F1.wireOp",EDGE,"E153"),sQuery(id+"F1.wireOp",EDGE,"E156"),sQuery(id+"F1.wireOp",EDGE,"E157"),sQuery(id+"F1.wireOp",EDGE,"E167"),sQuery(id+"F1.wireOp",EDGE,"E173"),sQuery(id+"F1.wireOp",EDGE,"E174"),sQuery(id+"F1.wireOp",EDGE,"E175"),sQuery(id+"F1.wireOp",EDGE,"E182"),sQuery(id+"F1.wireOp",EDGE,"E228"),sQuery(id+"F1.wireOp",EDGE,"E229")])]});
            var Q3;
            Q3=makeQuery(id+"F2.opExtrude","SWEPT_BODY",BODY,{"disambiguationData":[OSD([sQuery(id+"F1.wireOp",EDGE,"E132"),sQuery(id+"F1.wireOp",EDGE,"E139"),sQuery(id+"F1.wireOp",EDGE,"E156"),sQuery(id+"F1.wireOp",EDGE,"E241")])]});
            var Q4;
            Q4=makeQuery(id+"F2.opExtrude","SWEPT_BODY",BODY,{"disambiguationData":[OSD([sQuery(id+"F1.wireOp",EDGE,"E126.bottom"),sQuery(id+"F1.wireOp",EDGE,"E133"),sQuery(id+"F1.wireOp",EDGE,"E134"),sQuery(id+"F1.wireOp",EDGE,"E225"),sQuery(id+"F1.wireOp",EDGE,"E255"),sQuery(id+"F1.wireOp",EDGE,"E261")])]});
            transform(context, id + "F3", {"entities" : qUnion([Q0, Q1, Q2, Q3, Q4]), "transformType" : TransformType.TRANSLATION_3D, "dx" : 0 * mm, "dy" : 0 * mm, "dz" : 3 * mm, "makeCopy" : false});
        }
        {
            var Q0;
            Q0=makeQuery(id+"F1.imprint","IMPRINT",FACE,{"disambiguationData":[TD([[makeQuery(id+"F1.imprint","IMPRINT",EDGE,{"derivedFrom":sQuery(id+"F1.wireOp",EDGE,"E161.trimOffspring")}),1.0]])]});
            var Q1;
            {var subQ0=sQuery(id+"F1.wireOp",EDGE,"E261");Q1=makeQuery(id+"F1.imprint","IMPRINT",FACE,{"disambiguationData":[TD([[makeQuery(id+"F1.imprint","IMPRINT",EDGE,{"derivedFrom":subQ0}),1.0]])]});}
            extrude(context, id + "F4", {"entities" : qUnion([Q0, Q1]), "depth" : 9 * mm});
        }
        {
            var Q0;
            {var subQ6=sQuery(id+"F1.wireOp",EDGE,"E143");Q0=makeQuery(id+"F1.imprint","IMPRINT",FACE,{"disambiguationData":[TD([[makeQuery(id+"F1.imprint","IMPRINT",EDGE,{"derivedFrom":subQ6}),-1.0]])]});}
            var Q1;
            {var subQ0=sQuery(id+"F1.wireOp",EDGE,"E182");var subQ1=sQuery(id+"F1.wireOp",EDGE,"E153");var subQ2=makeQuery(id+"F1.imprint","INTERSECT",VERTEX,{"derivedFrom":[subQ1,subQ0]});Q1=makeQuery(id+"F1.imprint","IMPRINT",FACE,{"disambiguationData":[TD([[makeQuery(id+"F1.imprint","IMPRINT",EDGE,{"disambiguationData":[TD([[subQ2,-1.0]])],"derivedFrom":subQ1}),-1.0]])]});}
            var Q2;
            {var subQ3=sQuery(id+"F1.wireOp",EDGE,"E156");var subQ6=sQuery(id+"F1.wireOp",EDGE,"E267");var subQ8=makeQuery(id+"F1.imprint","INTERSECT",VERTEX,{"derivedFrom":[subQ3,subQ6]});Q2=makeQuery(id+"F1.imprint","IMPRINT",FACE,{"disambiguationData":[TD([[makeQuery(id+"F1.imprint","IMPRINT",EDGE,{"disambiguationData":[TD([[subQ8,-1.0]])],"derivedFrom":subQ3}),-1.0]])]});}
            var Q3;
            {var subQ0=sQuery(id+"F1.wireOp",EDGE,"E248");Q3=makeQuery(id+"F1.imprint","IMPRINT",FACE,{"disambiguationData":[TD([[makeQuery(id+"F1.imprint","IMPRINT",EDGE,{"derivedFrom":subQ0}),-1.0]])]});}
            var Q4;
            {var subQ0=sQuery(id+"F1.wireOp",EDGE,"E248");Q4=makeQuery(id+"F1.imprint","IMPRINT",FACE,{"disambiguationData":[TD([[makeQuery(id+"F1.imprint","IMPRINT",EDGE,{"derivedFrom":subQ0}),1.0]])]});}
            var Q5;
            {var subQ0=sQuery(id+"F1.wireOp",EDGE,"E232");Q5=makeQuery(id+"F1.imprint","IMPRINT",FACE,{"disambiguationData":[TD([[makeQuery(id+"F1.imprint","IMPRINT",EDGE,{"derivedFrom":subQ0}),-1.0]])]});}
            var Q6;
            {var subQ6=sQuery(id+"F1.wireOp",EDGE,"E230");var subQ8=sQuery(id+"F1.wireOp",EDGE,"E156");var subQ9=makeQuery(id+"F1.imprint","INTERSECT",VERTEX,{"derivedFrom":[subQ8,subQ6]});Q6=makeQuery(id+"F1.imprint","IMPRINT",FACE,{"disambiguationData":[TD([[makeQuery(id+"F1.imprint","IMPRINT",EDGE,{"disambiguationData":[TD([[subQ9,1.0]])],"derivedFrom":subQ8}),-1.0]])]});}
            var Q7;
            {var subQ3=sQuery(id+"F1.wireOp",EDGE,"E156");var subQ6=sQuery(id+"F1.wireOp",EDGE,"E230");var subQ7=makeQuery(id+"F1.imprint","INTERSECT",VERTEX,{"derivedFrom":[subQ3,subQ6]});Q7=makeQuery(id+"F1.imprint","IMPRINT",FACE,{"disambiguationData":[TD([[makeQuery(id+"F1.imprint","IMPRINT",EDGE,{"disambiguationData":[TD([[subQ7,-1.0]])],"derivedFrom":subQ3}),-1.0]])]});}
            var Q8;
            {var subQ1=sQuery(id+"F1.wireOp",EDGE,"E208");var subQ3=sQuery(id+"F1.wireOp",EDGE,"E230");var subQ4=makeQuery(id+"F1.imprint","INTERSECT",VERTEX,{"derivedFrom":[subQ1,subQ3]});Q8=makeQuery(id+"F1.imprint","IMPRINT",FACE,{"disambiguationData":[TD([[makeQuery(id+"F1.imprint","IMPRINT",EDGE,{"disambiguationData":[TD([[subQ4,-1.0]])],"derivedFrom":subQ3}),-1.0]])]});}
            var Q9;
            {var subQ0=sQuery(id+"F1.wireOp",EDGE,"E207");var subQ1=sQuery(id+"F1.wireOp",EDGE,"E156");var subQ2=makeQuery(id+"F1.imprint","INTERSECT",VERTEX,{"derivedFrom":[subQ1,subQ0]});Q9=makeQuery(id+"F1.imprint","IMPRINT",FACE,{"disambiguationData":[TD([[makeQuery(id+"F1.imprint","IMPRINT",EDGE,{"disambiguationData":[TD([[subQ2,-1.0]])],"derivedFrom":subQ1}),-1.0]])]});}
            var Q10;
            Q10=makeQuery(id+"F1.imprint","IMPRINT",FACE,{"disambiguationData":[TD([[makeQuery(id+"F1.imprint","IMPRINT",EDGE,{"derivedFrom":sQuery(id+"F1.wireOp",EDGE,"E169")}),1.0]])]});
            var Q11;
            Q11=makeQuery(id+"F1.imprint","IMPRINT",FACE,{"disambiguationData":[TD([[makeQuery(id+"F1.imprint","IMPRINT",EDGE,{"derivedFrom":sQuery(id+"F1.wireOp",EDGE,"E169")}),-1.0]])]});
            var Q12;
            {var subQ0=sQuery(id+"F1.wireOp",EDGE,"E165");var subQ1=sQuery(id+"F1.wireOp",EDGE,"E156");var subQ2=makeQuery(id+"F1.imprint","INTERSECT",VERTEX,{"derivedFrom":[subQ1,subQ0]});Q12=makeQuery(id+"F1.imprint","IMPRINT",FACE,{"disambiguationData":[TD([[makeQuery(id+"F1.imprint","IMPRINT",EDGE,{"disambiguationData":[TD([[subQ2,-1.0]])],"derivedFrom":subQ1}),-1.0]])]});}
            var Q13;
            {var subQ0=sQuery(id+"F1.wireOp",EDGE,"E269");var subQ1=sQuery(id+"F1.wireOp",EDGE,"E208");var subQ2=makeQuery(id+"F1.imprint","INTERSECT",VERTEX,{"derivedFrom":[subQ1,subQ0]});Q13=makeQuery(id+"F1.imprint","IMPRINT",FACE,{"disambiguationData":[TD([[makeQuery(id+"F1.imprint","IMPRINT",EDGE,{"disambiguationData":[TD([[subQ2,1.0]])],"derivedFrom":subQ1}),-1.0]])]});}
            var Q14;
            {var subQ3=sQuery(id+"F1.wireOp",EDGE,"E255");var subQ7=sQuery(id+"F1.wireOp",EDGE,"E133");var subQ9=makeQuery(id+"F1.imprint","INTERSECT",VERTEX,{"derivedFrom":[subQ7,subQ3]});Q14=makeQuery(id+"F1.imprint","IMPRINT",FACE,{"disambiguationData":[TD([[makeQuery(id+"F1.imprint","IMPRINT",EDGE,{"disambiguationData":[TD([[subQ9,1.0]])],"derivedFrom":subQ3}),-1.0]])]});}
            var Q15;
            {var subQ1=sQuery(id+"F1.wireOp",EDGE,"E132");var subQ3=sQuery(id+"F1.wireOp",EDGE,"E156");var subQ4=makeQuery(id+"F1.imprint","INTERSECT",VERTEX,{"derivedFrom":[subQ1,subQ3]});Q15=makeQuery(id+"F1.imprint","IMPRINT",FACE,{"disambiguationData":[TD([[makeQuery(id+"F1.imprint","IMPRINT",EDGE,{"disambiguationData":[TD([[subQ4,-1.0]])],"derivedFrom":subQ3}),-1.0]])]});}
            var Q16;
            {var subQ1=sQuery(id+"F1.wireOp",EDGE,"E196");var subQ3=sQuery(id+"F1.wireOp",EDGE,"E255");var subQ4=makeQuery(id+"F1.imprint","INTERSECT",VERTEX,{"derivedFrom":[subQ1,subQ3]});Q16=makeQuery(id+"F1.imprint","IMPRINT",FACE,{"disambiguationData":[TD([[makeQuery(id+"F1.imprint","IMPRINT",EDGE,{"disambiguationData":[TD([[subQ4,-1.0]])],"derivedFrom":subQ3}),-1.0]])]});}
            var Q17;
            {var subQ1=sQuery(id+"F1.wireOp",EDGE,"E204");var subQ3=sQuery(id+"F1.wireOp",EDGE,"E255");var subQ4=makeQuery(id+"F1.imprint","INTERSECT",VERTEX,{"derivedFrom":[subQ1,subQ3]});Q17=makeQuery(id+"F1.imprint","IMPRINT",FACE,{"disambiguationData":[TD([[makeQuery(id+"F1.imprint","IMPRINT",EDGE,{"disambiguationData":[TD([[subQ4,-1.0]])],"derivedFrom":subQ3}),-1.0]])]});}
            var Q18;
            {var subQ1=sQuery(id+"F1.wireOp",EDGE,"E127.right");Q18=makeQuery(id+"F1.imprint","IMPRINT",FACE,{"disambiguationData":[TD([[makeQuery(id+"F1.imprint","IMPRINT",EDGE,{"derivedFrom":subQ1}),-1.0]])]});}
            var Q19;
            {var subQ0=sQuery(id+"F1.wireOp",EDGE,"E127.right");Q19=makeQuery(id+"F1.imprint","IMPRINT",FACE,{"disambiguationData":[TD([[makeQuery(id+"F1.imprint","IMPRINT",EDGE,{"derivedFrom":subQ0}),1.0]])]});}
            var Q20;
            {var subQ5=sQuery(id+"F1.wireOp",EDGE,"E275");Q20=makeQuery(id+"F1.imprint","IMPRINT",FACE,{"disambiguationData":[TD([[makeQuery(id+"F1.imprint","IMPRINT",EDGE,{"derivedFrom":subQ5}),1.0]])]});}
            var Q21;
            {var subQ5=sQuery(id+"F1.wireOp",EDGE,"E275");Q21=makeQuery(id+"F1.imprint","IMPRINT",FACE,{"disambiguationData":[TD([[makeQuery(id+"F1.imprint","IMPRINT",EDGE,{"derivedFrom":subQ5}),1.0]])]});}
            var Q22;
            {var subQ23=sQuery(id+"F1.wireOp",EDGE,"E157");Q22=makeQuery(id+"F1.imprint","IMPRINT",FACE,{"disambiguationData":[TD([[makeQuery(id+"F1.imprint","IMPRINT",EDGE,{"derivedFrom":subQ23}),1.0]])]});}
            extrude(context, id + "F5", {"entities" : qUnion([Q0, Q1, Q2, Q3, Q4, Q5, Q6, Q7, Q8, Q9, Q10, Q11, Q12, Q13, Q14, Q15, Q16, Q17, Q18, Q19, Q20, Q21, Q22]), "depth" : 3 * mm});
        }
        {
            var Q0;
            Q0=makeQuery(id+"F5.opExtrude","SWEPT_BODY",BODY,{"disambiguationData":[OSD([sQuery(id+"F1.wireOp",EDGE,"E149"),sQuery(id+"F1.wireOp",EDGE,"E150"),sQuery(id+"F1.wireOp",EDGE,"E151"),sQuery(id+"F1.wireOp",EDGE,"E153"),sQuery(id+"F1.wireOp",EDGE,"E156"),sQuery(id+"F1.wireOp",EDGE,"E157"),sQuery(id+"F1.wireOp",EDGE,"E161.trimOffspring"),sQuery(id+"F1.wireOp",EDGE,"E162"),sQuery(id+"F1.wireOp",EDGE,"E208"),sQuery(id+"F1.wireOp",EDGE,"E212"),sQuery(id+"F1.wireOp",EDGE,"E213"),sQuery(id+"F1.wireOp",EDGE,"E230"),sQuery(id+"F1.wireOp",EDGE,"E233"),sQuery(id+"F1.wireOp",EDGE,"E234"),sQuery(id+"F1.wireOp",EDGE,"E253"),sQuery(id+"F1.wireOp",EDGE,"E255"),sQuery(id+"F1.wireOp",EDGE,"E256")])]});
            transform(context, id + "F6", {"entities" : qUnion([Q0]), "transformType" : TransformType.TRANSLATION_3D, "dx" : 0 * mm, "dy" : 0 * mm, "dz" : 3 * mm, "makeCopy" : false});
        }
        {
            var Q0;
            Q0=makeQuery(id+"F1.imprint","IMPRINT",FACE,{"disambiguationData":[TD([[makeQuery(id+"F1.imprint","IMPRINT",EDGE,{"derivedFrom":sQuery(id+"F1.wireOp",EDGE,"E126.left")}),-1.0]])]});
            var Q1;
            {var subQ0=sQuery(id+"F1.wireOp",EDGE,"E221");Q1=makeQuery(id+"F1.imprint","IMPRINT",FACE,{"disambiguationData":[TD([[makeQuery(id+"F1.imprint","IMPRINT",EDGE,{"derivedFrom":subQ0}),-1.0]])]});}
            var Q2;
            {var subQ0=sQuery(id+"F1.wireOp",EDGE,"E223");Q2=makeQuery(id+"F1.imprint","IMPRINT",FACE,{"disambiguationData":[TD([[makeQuery(id+"F1.imprint","IMPRINT",EDGE,{"derivedFrom":subQ0}),1.0]])]});}
            var Q3;
            {var subQ3=sQuery(id+"F1.wireOp",EDGE,"E140");var subQ5=sQuery(id+"F1.wireOp",EDGE,"E200");var subQ6=makeQuery(id+"F1.imprint","INTERSECT",VERTEX,{"derivedFrom":[subQ3,subQ5]});Q3=makeQuery(id+"F1.imprint","IMPRINT",FACE,{"disambiguationData":[TD([[makeQuery(id+"F1.imprint","IMPRINT",EDGE,{"disambiguationData":[TD([[subQ6,-1.0]])],"derivedFrom":subQ3}),1.0]])]});}
            var Q4;
            {var subQ0=sQuery(id+"F1.wireOp",EDGE,"E219");Q4=makeQuery(id+"F1.imprint","IMPRINT",FACE,{"disambiguationData":[TD([[makeQuery(id+"F1.imprint","IMPRINT",EDGE,{"derivedFrom":subQ0}),1.0]])]});}
            var Q5;
            {var subQ0=sQuery(id+"F1.wireOp",EDGE,"E217");var subQ1=sQuery(id+"F1.wireOp",EDGE,"E202");var subQ2=makeQuery(id+"F1.imprint","INTERSECT",VERTEX,{"derivedFrom":[subQ1,subQ0]});Q5=makeQuery(id+"F1.imprint","IMPRINT",FACE,{"disambiguationData":[TD([[makeQuery(id+"F1.imprint","IMPRINT",EDGE,{"disambiguationData":[TD([[subQ2,-1.0]])],"derivedFrom":subQ1}),-1.0]])]});}
            var Q6;
            {var subQ3=sQuery(id+"F1.wireOp",EDGE,"E196");var subQ5=sQuery(id+"F1.wireOp",EDGE,"E202");var subQ6=makeQuery(id+"F1.imprint","INTERSECT",VERTEX,{"derivedFrom":[subQ3,subQ5]});Q6=makeQuery(id+"F1.imprint","IMPRINT",FACE,{"disambiguationData":[TD([[makeQuery(id+"F1.imprint","IMPRINT",EDGE,{"disambiguationData":[TD([[subQ6,-1.0]])],"derivedFrom":subQ3}),-1.0]])]});}
            var Q7;
            {var subQ9=sQuery(id+"F1.wireOp",EDGE,"E175");Q7=makeQuery(id+"F1.imprint","IMPRINT",FACE,{"disambiguationData":[TD([[makeQuery(id+"F1.imprint","IMPRINT",EDGE,{"derivedFrom":subQ9}),1.0]])]});}
            var Q8;
            {var subQ0=sQuery(id+"F1.wireOp",EDGE,"E281");var subQ5=sQuery(id+"F1.wireOp",EDGE,"E280");var subQ6=makeQuery(id+"F1.imprint","INTERSECT",VERTEX,{"derivedFrom":[subQ5,subQ0]});Q8=makeQuery(id+"F1.imprint","IMPRINT",FACE,{"disambiguationData":[TD([[makeQuery(id+"F1.imprint","IMPRINT",EDGE,{"disambiguationData":[TD([[subQ6,-1.0]])],"derivedFrom":subQ5}),1.0]])]});}
            var Q9;
            {var subQ0=sQuery(id+"F1.wireOp",EDGE,"E281");var subQ1=sQuery(id+"F1.wireOp",EDGE,"E280");var subQ2=makeQuery(id+"F1.imprint","INTERSECT",VERTEX,{"derivedFrom":[subQ1,subQ0]});Q9=makeQuery(id+"F1.imprint","IMPRINT",FACE,{"disambiguationData":[TD([[makeQuery(id+"F1.imprint","IMPRINT",EDGE,{"disambiguationData":[TD([[subQ2,-1.0]])],"derivedFrom":subQ1}),-1.0]])]});}
            var Q10;
            {var subQ0=sQuery(id+"F1.wireOp",EDGE,"E284");var subQ1=sQuery(id+"F1.wireOp",EDGE,"E280");var subQ2=makeQuery(id+"F1.imprint","INTERSECT",VERTEX,{"derivedFrom":[subQ1,subQ0]});Q10=makeQuery(id+"F1.imprint","IMPRINT",FACE,{"disambiguationData":[TD([[makeQuery(id+"F1.imprint","IMPRINT",EDGE,{"disambiguationData":[TD([[subQ2,-1.0]])],"derivedFrom":subQ1}),-1.0]])]});}
            var Q11;
            {var subQ0=sQuery(id+"F1.wireOp",EDGE,"E283");var subQ5=sQuery(id+"F1.wireOp",EDGE,"E280");var subQ6=makeQuery(id+"F1.imprint","INTERSECT",VERTEX,{"derivedFrom":[subQ5,subQ0]});Q11=makeQuery(id+"F1.imprint","IMPRINT",FACE,{"disambiguationData":[TD([[makeQuery(id+"F1.imprint","IMPRINT",EDGE,{"disambiguationData":[TD([[subQ6,1.0]])],"derivedFrom":subQ5}),1.0]])]});}
            var Q12;
            {var subQ0=sQuery(id+"F1.wireOp",EDGE,"E283");var subQ1=sQuery(id+"F1.wireOp",EDGE,"E280");var subQ2=makeQuery(id+"F1.imprint","INTERSECT",VERTEX,{"derivedFrom":[subQ1,subQ0]});Q12=makeQuery(id+"F1.imprint","IMPRINT",FACE,{"disambiguationData":[TD([[makeQuery(id+"F1.imprint","IMPRINT",EDGE,{"disambiguationData":[TD([[subQ2,1.0]])],"derivedFrom":subQ1}),-1.0]])]});}
            extrude(context, id + "F7", {"entities" : qUnion([Q0, Q1, Q2, Q3, Q4, Q5, Q6, Q7, Q8, Q9, Q10, Q11, Q12]), "depth" : 9 * mm});
        }
    });
